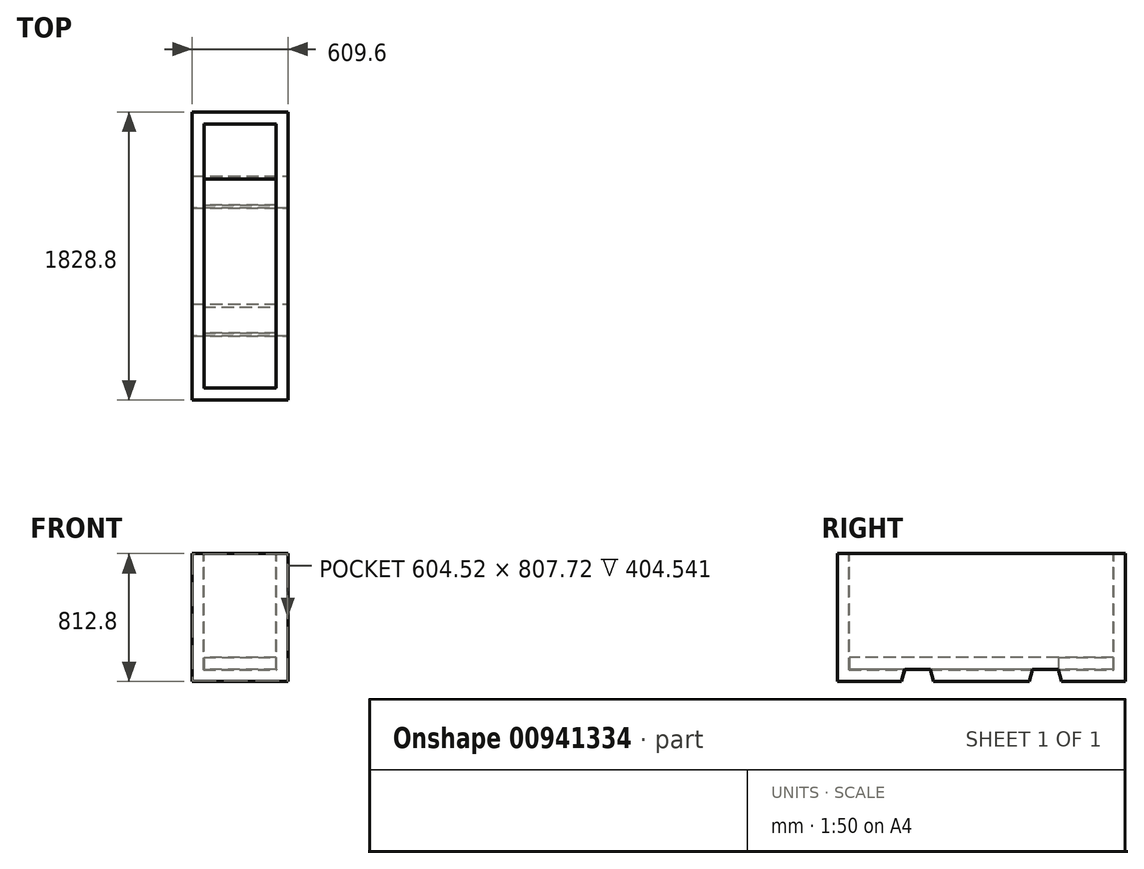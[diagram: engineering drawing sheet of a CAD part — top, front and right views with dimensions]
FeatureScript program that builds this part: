
annotation { "Feature Type Name" : "Feature", "Feature Type Description" : "" }
export const myFeature = defineFeature(function(context is Context, id is Id, definition is map)
    precondition{}
    {
        {
            var Q0;
            Q0=qCreatedBy(makeId("Front.planeOp"),FACE);
            var sketch = newSketch(context, id + "F0", { "sketchPlane" : qUnion([Q0])});
            skLineSegment(sketch, "E0.bottom", {"start": v(304.8, -406.4) * mm, "end": v(-304.8, -406.4) * mm});
            skLineSegment(sketch, "E0.top", {"start": v(304.8, 406.4) * mm, "end": v(-304.8, 406.4) * mm});
            skLineSegment(sketch, "E0.left", {"start": v(304.8, -406.4) * mm, "end": v(304.8, 406.4) * mm});
            skLineSegment(sketch, "E0.right", {"start": v(-304.8, -406.4) * mm, "end": v(-304.8, 406.4) * mm});
            skPoint(sketch, "E0.middle", {"position": v(0, 0) * mm});
            skSolve(sketch);
        }
        {
            var Q0;
            Q0=makeQuery(id+"F0.imprint","IMPRINT",FACE,{"disambiguationData":[TD([[makeQuery(id+"F0.imprint","IMPRINT",EDGE,{"derivedFrom":sQuery(id+"F0.wireOp",EDGE,"E0.bottom")}),-1.0]])]});
            extrude(context, id + "F1", {"entities" : qUnion([Q0]), "depth" : 1828.8 * mm, "offsetDistance" : 25.4 * mm});
        }
        {
            var Q0;
            Q0=makeQuery(id+"F1.opExtrude","SWEPT_FACE",FACE,{"disambiguationData":[OSD([sQuery(id+"F0.wireOp",EDGE,"E0.top")])]});
            shell(context, id + "F2", {"entities" : qUnion([Q0]), "thickness" : 76.2 * mm});
        }
        {
            var Q0;
            Q0=makeQuery(id+"F1.opExtrude","SWEPT_FACE",FACE,{"disambiguationData":[OSD([sQuery(id+"F0.wireOp",EDGE,"E0.left")])]});
            var sketch = newSketch(context, id + "F3", { "sketchPlane" : qUnion([Q0])});
            skLineSegment(sketch, "E1", {"start": v(-914.4, 468.2) * mm, "end": v(-914.4, -475.56) * mm, "construction": true});
            skLineSegment(sketch, "E2", {"start": v(-609.6, 463.7) * mm, "end": v(-609.6, -480.06) * mm, "construction": true});
            skLineSegment(sketch, "E3", {"start": v(-1219.2, 466.24) * mm, "end": v(-1219.2, -477.52) * mm, "construction": true});
            skLineSegment(sketch, "E4", {"start": v(-1219.2, -406.4) * mm, "end": v(-1239.62, -330.2) * mm});
            skLineSegment(sketch, "E5", {"start": v(-1239.62, -330.2) * mm, "end": v(-1401.98, -330.2) * mm});
            skLineSegment(sketch, "E6", {"start": v(-1401.98, -330.2) * mm, "end": v(-1422.4, -406.4) * mm});
            skLineSegment(sketch, "E7", {"start": v(-1422.4, -406.4) * mm, "end": v(-1219.2, -406.4) * mm});
            skLineSegment(sketch, "E8", {"start": v(-406.4, -406.4) * mm, "end": v(-426.82, -330.2) * mm});
            skLineSegment(sketch, "E9", {"start": v(-589.18, -330.2) * mm, "end": v(-609.6, -406.4) * mm});
            skLineSegment(sketch, "E10", {"start": v(-609.6, -406.4) * mm, "end": v(-406.4, -406.4) * mm});
            skLineSegment(sketch, "E11", {"start": v(-589.18, -330.2) * mm, "end": v(-426.82, -330.2) * mm});
            skSolve(sketch);
        }
        {
            var Q0;
            Q0=makeQuery(id+"F1.opExtrude","SWEPT_FACE",FACE,{"disambiguationData":[OSD([sQuery(id+"F0.wireOp",EDGE,"E0.left")])]});
            var Q1;
            Q1=makeQuery(id+"F1.opExtrude","SWEPT_BODY",BODY,{"disambiguationData":[OSD([sQuery(id+"F0.wireOp",EDGE,"E0.bottom"),sQuery(id+"F0.wireOp",EDGE,"E0.top"),sQuery(id+"F0.wireOp",EDGE,"E0.left"),sQuery(id+"F0.wireOp",EDGE,"E0.right")])]});
            shell(context, id + "F4", {"isHollow" : true, "entities" : qUnion([Q0]), "parts" : qUnion([Q1]), "thickness" : 2.54 * mm});
        }
        {
            var Q0;
            Q0=makeQuery(id+"F3.imprint","IMPRINT",FACE,{"disambiguationData":[TD([[makeQuery(id+"F3.imprint","IMPRINT",EDGE,{"derivedFrom":sQuery(id+"F3.wireOp",EDGE,"E4")}),1.0]])]});
            var Q1;
            Q1=makeQuery(id+"F3.imprint","IMPRINT",FACE,{"disambiguationData":[TD([[makeQuery(id+"F3.imprint","IMPRINT",EDGE,{"derivedFrom":sQuery(id+"F3.wireOp",EDGE,"E8")}),1.0]])]});
            extrude(context, id + "F5", {"entities" : qUnion([Q0, Q1]), "operationType" : NewBodyOperationType.REMOVE, "oppositeDirection" : true, "depth" : 609.6 * mm, "offsetDistance" : 25.4 * mm});
        }
        {
            var Q0;
            {var subQ3=sQuery(id+"F0.wireOp",EDGE,"E0.bottom");Q0=makeQuery(id+"F5.boolean.opBoolean","SPLIT",FACE,{"disambiguationData":[TD([makeQuery(id+"F5.opExtrude","SWEPT_FACE",FACE,{"disambiguationData":[OSD([sQuery(id+"F3.wireOp",EDGE,"E8")])]})])],"derivedFrom":makeQuery(id+"F2.opShell","OFFSET_FACE",FACE,{"disambiguationData":[OSD([subQ3])]})});}
            var sketch = newSketch(context, id + "F6", { "sketchPlane" : qUnion([Q0])});
            skLineSegment(sketch, "E12.bottom", {"start": v(228.6, -76.2) * mm, "end": v(-229.52, -76.2) * mm});
            skLineSegment(sketch, "E12.top", {"start": v(228.6, -1753.37) * mm, "end": v(-229.52, -1753.37) * mm});
            skLineSegment(sketch, "E12.left", {"start": v(228.6, -76.2) * mm, "end": v(228.6, -1753.37) * mm});
            skLineSegment(sketch, "E12.right", {"start": v(-229.52, -76.2) * mm, "end": v(-229.52, -1753.37) * mm});
            skSolve(sketch);
        }
        {
            var Q0;
            {var subQ7=sQuery(id+"F0.wireOp",EDGE,"E0.bottom");var subQ8=sQuery(id+"F3.wireOp",EDGE,"E8");var subQ9=makeQuery(id+"F5.opExtrude","SWEPT_FACE",FACE,{"disambiguationData":[OSD([subQ8])]});var subQ10=makeQuery(id+"F2.opShell","OFFSET_FACE",FACE,{"disambiguationData":[OSD([subQ7])]});var subQ11=sQuery(id+"F3.wireOp",EDGE,"E11");var subQ13=makeQuery(id+"F5.boolean.opBoolean","COPY",EDGE,{"disambiguationData":[topologyDisambiguationEdgeConnected([subQ10,subQ9])],"derivedFrom":makeQuery(id+"F5.opExtrude","SWEPT_EDGE",EDGE,{"disambiguationData":[OSD([subQ8,subQ11])]})});Q0=makeQuery(id+"F6.imprint","IMPRINT",FACE,{"disambiguationData":[TD([[makeQuery(id+"F6.imprint","IMPRINT",EDGE,{"derivedFrom":subQ13}),1.0]])]});}
            var Q1;
            {var subQ8=sQuery(id+"F6.wireOp",EDGE,"E12.top");Q1=makeQuery(id+"F6.imprint","IMPRINT",FACE,{"disambiguationData":[TD([[makeQuery(id+"F6.imprint","IMPRINT",EDGE,{"derivedFrom":subQ8}),-1.0]])]});}
            var Q2;
            Q2=sQuery(id+"F6.wireOp",EDGE,"E12.left");
            var Q3;
            Q3=sQuery(id+"F6.wireOp",EDGE,"E12.bottom");
            var Q4;
            Q4=sQuery(id+"F6.wireOp",EDGE,"E12.right");
            var Q5;
            Q5=sQuery(id+"F6.wireOp",EDGE,"E12.top");
            extrude(context, id + "F7", {"entities" : qUnion([Q0, Q1]), "surfaceEntities" : qUnion([Q2, Q3, Q4, Q5]), "depth" : 76.2 * mm, "offsetDistance" : 25.4 * mm});
        }
    });
